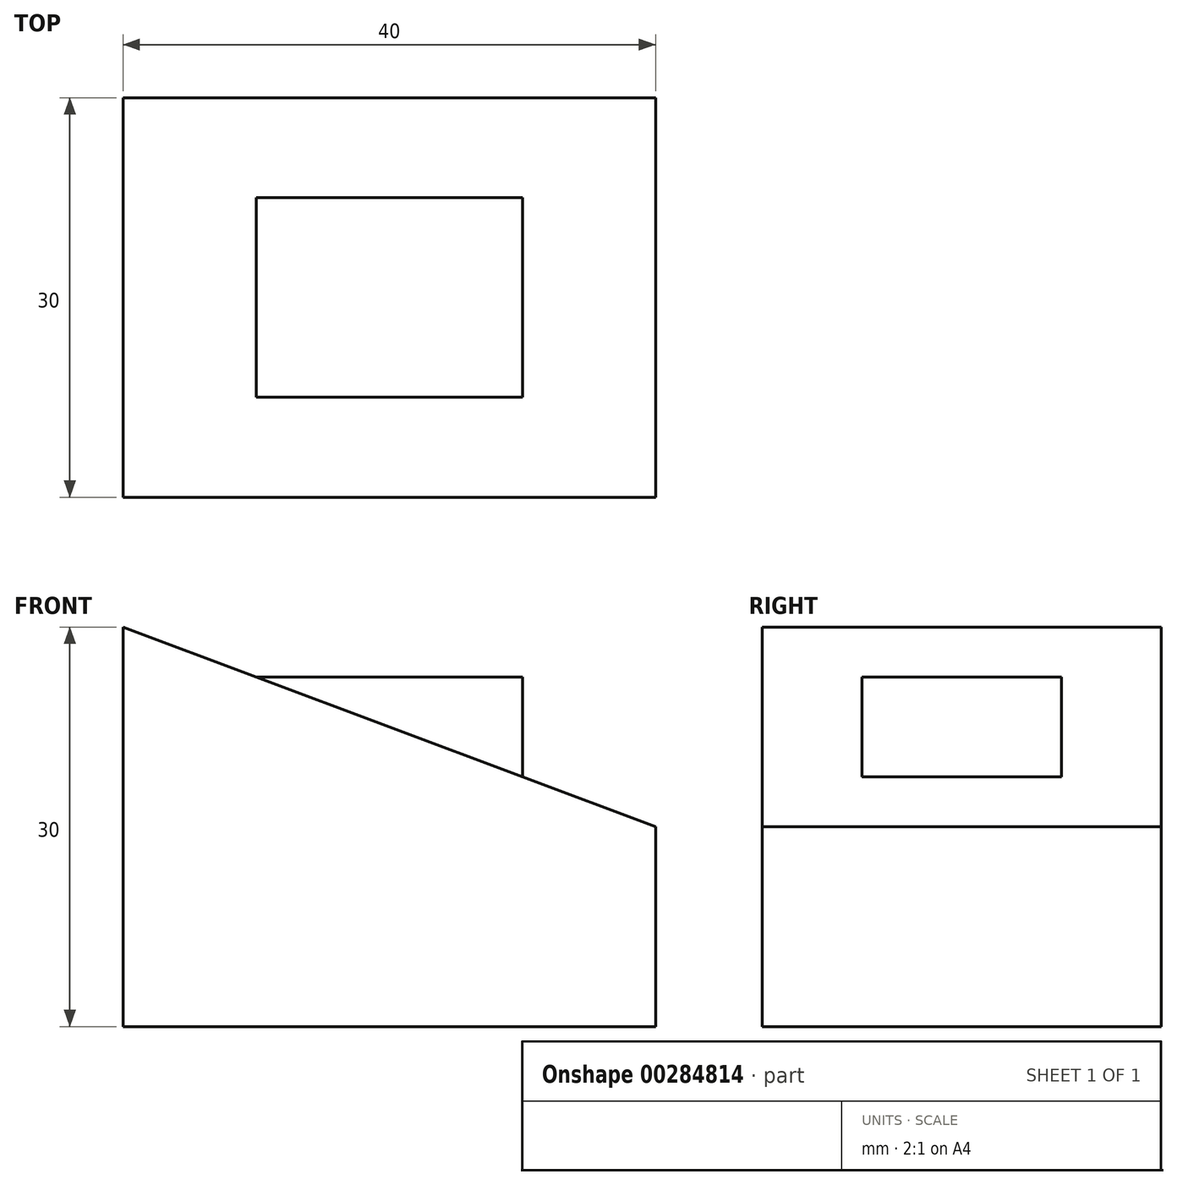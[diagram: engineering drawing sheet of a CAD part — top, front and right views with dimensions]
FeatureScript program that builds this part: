
annotation { "Feature Type Name" : "Feature", "Feature Type Description" : "" }
export const myFeature = defineFeature(function(context is Context, id is Id, definition is map)
    precondition{}
    {
        {
            var Q0;
            Q0=qCreatedBy(makeId("Front.planeOp"),FACE);
            var sketch = newSketch(context, id + "F0", { "sketchPlane" : qUnion([Q0])});
            skLineSegment(sketch, "E0.bottom", {"start": v(0, 0) * mm, "end": v(40, 0) * mm});
            skLineSegment(sketch, "E0.top", {"start": v(0, 30) * mm, "end": v(40, 30) * mm});
            skLineSegment(sketch, "E0.left", {"start": v(0, 0) * mm, "end": v(0, 30) * mm});
            skLineSegment(sketch, "E0.right", {"start": v(40, 0) * mm, "end": v(40, 30) * mm});
            skLineSegment(sketch, "E1", {"start": v(0, 30) * mm, "end": v(40, 15) * mm});
            skLineSegment(sketch, "E2.bottom", {"start": v(10, 26.25) * mm, "end": v(30, 26.25) * mm});
            skLineSegment(sketch, "E2.top", {"start": v(10, 18.75) * mm, "end": v(30, 18.75) * mm});
            skLineSegment(sketch, "E2.left", {"start": v(10, 26.25) * mm, "end": v(10, 18.75) * mm});
            skLineSegment(sketch, "E2.right", {"start": v(30, 26.25) * mm, "end": v(30, 18.75) * mm});
            skSolve(sketch);
        }
        {
            var Q0;
            {var subQ4=sQuery(id+"F0.wireOp",EDGE,"E0.bottom");Q0=makeQuery(id+"F0.imprint","IMPRINT",FACE,{"disambiguationData":[TD([[makeQuery(id+"F0.imprint","IMPRINT",EDGE,{"derivedFrom":subQ4}),1.0]])]});}
            var Q1;
            {var subQ2=sQuery(id+"F0.wireOp",EDGE,"E2.top");Q1=makeQuery(id+"F0.imprint","IMPRINT",FACE,{"disambiguationData":[TD([[makeQuery(id+"F0.imprint","IMPRINT",EDGE,{"derivedFrom":subQ2}),1.0]])]});}
            extrude(context, id + "F1", {"entities" : qUnion([Q0, Q1]), "depth" : 30 * mm, "symmetric" : true});
        }
        {
            var Q0;
            {var subQ0=sQuery(id+"F0.wireOp",EDGE,"E2.bottom");Q0=makeQuery(id+"F0.imprint","IMPRINT",FACE,{"disambiguationData":[TD([[makeQuery(id+"F0.imprint","IMPRINT",EDGE,{"derivedFrom":subQ0}),-1.0]])]});}
            extrude(context, id + "F2", {"entities" : qUnion([Q0]), "operationType" : NewBodyOperationType.ADD, "oppositeDirection" : true, "depth" : 15 * mm, "symmetric" : true});
        }
    });
